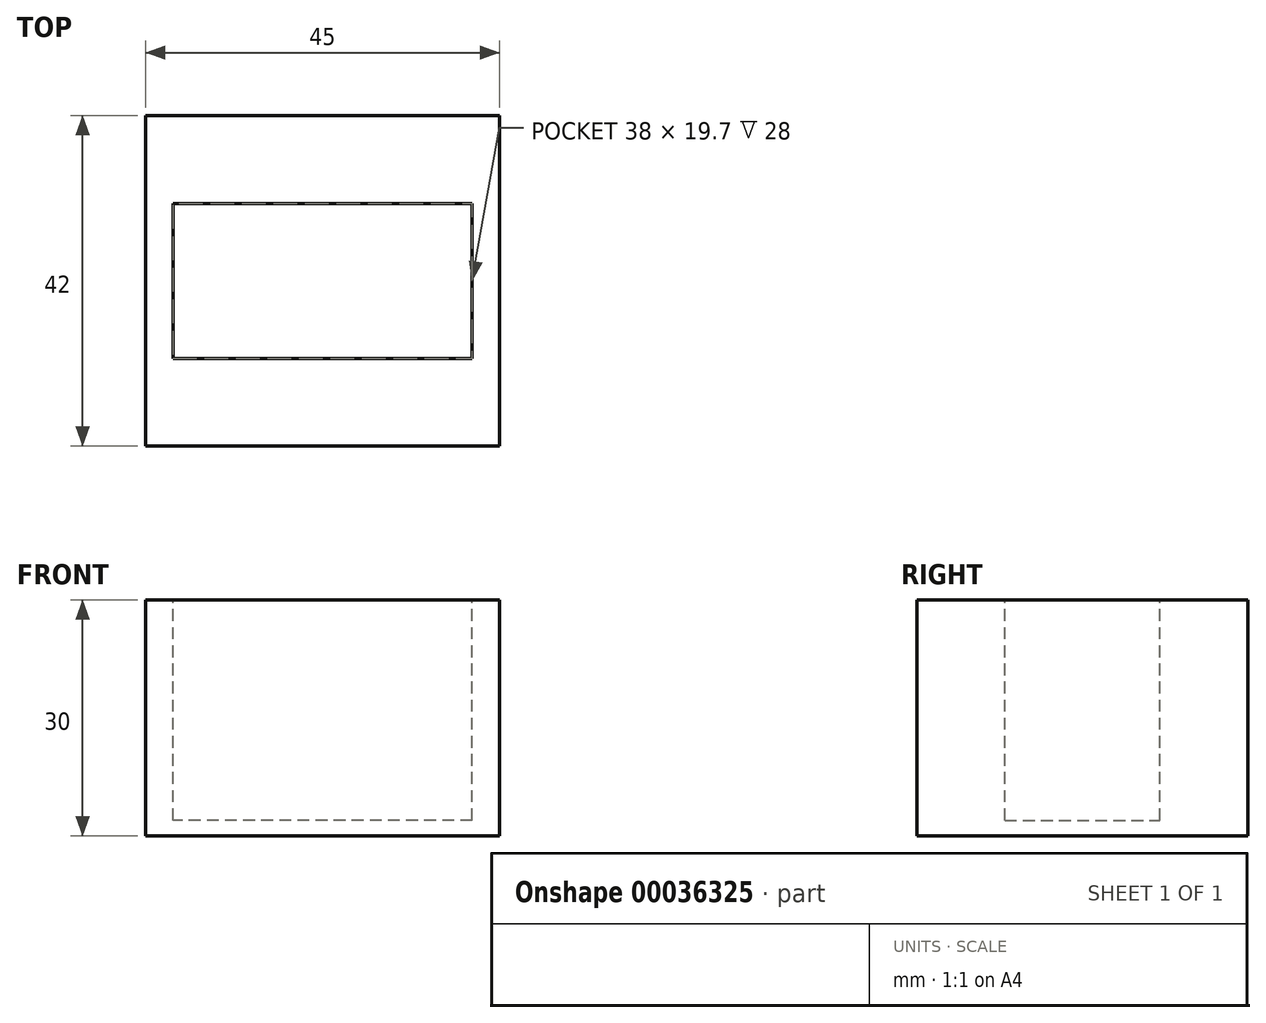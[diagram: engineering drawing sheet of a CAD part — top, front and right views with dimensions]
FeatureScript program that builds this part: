
annotation { "Feature Type Name" : "Feature", "Feature Type Description" : "" }
export const myFeature = defineFeature(function(context is Context, id is Id, definition is map)
    precondition{}
    {
        {
            var Q0;
            Q0=qCreatedBy(makeId("Top.planeOp"),FACE);
            var sketch = newSketch(context, id + "F0", { "sketchPlane" : qUnion([Q0])});
            skLineSegment(sketch, "E0.rect.bottom", {"start": v(19, -9.85) * mm, "end": v(-19, -9.85) * mm});
            skLineSegment(sketch, "E0.rect.top", {"start": v(19, 9.85) * mm, "end": v(-19, 9.85) * mm});
            skLineSegment(sketch, "E0.rect.left", {"start": v(19, -9.85) * mm, "end": v(19, 9.85) * mm});
            skLineSegment(sketch, "E0.rect.right", {"start": v(-19, -9.85) * mm, "end": v(-19, 9.85) * mm});
            skPoint(sketch, "E0.rect.middle", {"position": v(0, 0) * mm});
            skSolve(sketch);
        }
        {
            var Q0;
            Q0=qCreatedBy(makeId("Top.planeOp"),FACE);
            var sketch = newSketch(context, id + "F1", { "sketchPlane" : qUnion([Q0])});
            skLineSegment(sketch, "E1.rect.bottom", {"start": v(22.5, -21) * mm, "end": v(-22.5, -21) * mm});
            skLineSegment(sketch, "E1.rect.top", {"start": v(22.5, 21) * mm, "end": v(-22.5, 21) * mm});
            skLineSegment(sketch, "E1.rect.left", {"start": v(22.5, -21) * mm, "end": v(22.5, 21) * mm});
            skLineSegment(sketch, "E1.rect.right", {"start": v(-22.5, -21) * mm, "end": v(-22.5, 21) * mm});
            skPoint(sketch, "E1.rect.middle", {"position": v(0, 0) * mm});
            skSolve(sketch);
        }
        {
            var Q0;
            Q0 = qSketchRegion(id + "F1", true);
            extrude(context, id + "F2", {"entities" : qUnion([Q0]), "oppositeDirection" : true, "depth" : 30 * mm});
        }
        {
            var Q0;
            Q0 = qSketchRegion(id + "F0", true);
            extrude(context, id + "F3", {"entities" : qUnion([Q0]), "operationType" : NewBodyOperationType.REMOVE, "oppositeDirection" : true, "depth" : 28 * mm});
        }
    });
